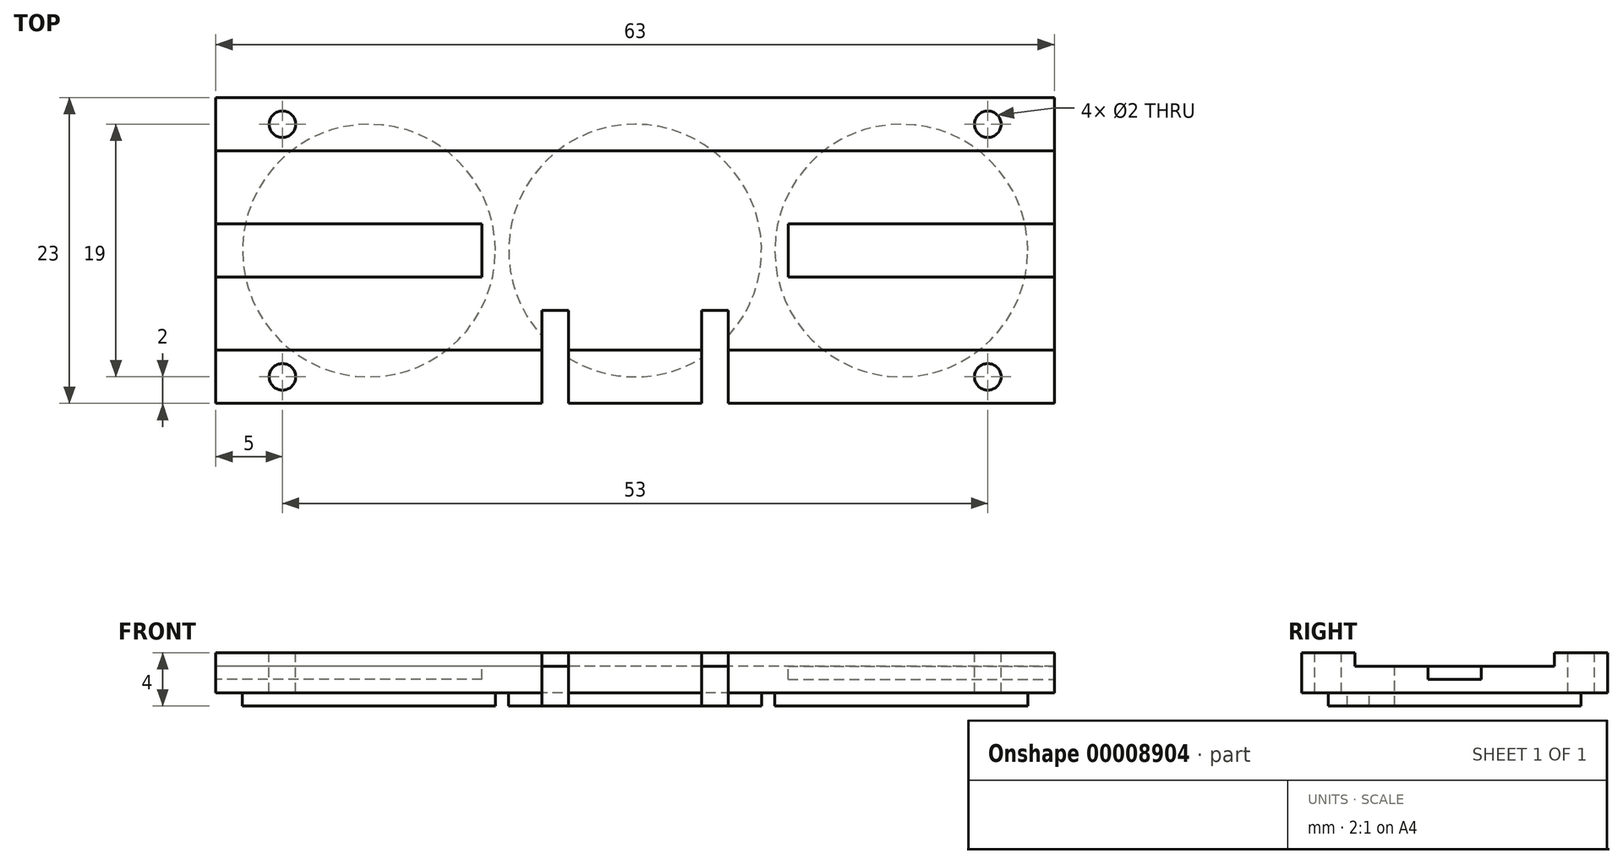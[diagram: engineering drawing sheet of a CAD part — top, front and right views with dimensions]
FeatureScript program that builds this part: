
annotation { "Feature Type Name" : "Feature", "Feature Type Description" : "" }
export const myFeature = defineFeature(function(context is Context, id is Id, definition is map)
    precondition{}
    {
        {
            var Q0;
            Q0=qCreatedBy(makeId("Top.planeOp"),FACE);
            var sketch = newSketch(context, id + "F0", { "sketchPlane" : qUnion([Q0])});
            skLineSegment(sketch, "E0.0", {"start": v(0, 12) * mm, "end": v(-32, 12) * mm, "construction": true});
            skLineSegment(sketch, "E1.0", {"start": v(0, 12) * mm, "end": v(32, 12) * mm, "construction": true});
            skLineSegment(sketch, "E2.0", {"start": v(0, -12) * mm, "end": v(-32, -12) * mm, "construction": true});
            skLineSegment(sketch, "E3.0", {"start": v(0, -12) * mm, "end": v(32, -12) * mm, "construction": true});
            skLineSegment(sketch, "E4", {"start": v(-32, 12) * mm, "end": v(-32, -12) * mm, "construction": true});
            skLineSegment(sketch, "E5", {"start": v(32, 12) * mm, "end": v(32, -12) * mm, "construction": true});
            skCircle(sketch, "E6", {"center": v(0, 0) * mm, "radius": 10 * mm, "construction": true});
            skLineSegment(sketch, "E7", {"start": v(0, 0) * mm, "end": v(-20, 0) * mm, "construction": true});
            skLineSegment(sketch, "E8", {"start": v(0, 0) * mm, "end": v(20, 0) * mm, "construction": true});
            skCircle(sketch, "E9", {"center": v(-20, 0) * mm, "radius": 10 * mm, "construction": true});
            skCircle(sketch, "E10", {"center": v(20, 0) * mm, "radius": 10 * mm, "construction": true});
            skLineSegment(sketch, "E11.0", {"start": v(-31.5, 12) * mm, "end": v(-31.5, -12) * mm});
            skLineSegment(sketch, "E12.0", {"start": v(31.5, 12) * mm, "end": v(31.5, -12) * mm});
            skLineSegment(sketch, "E13.0", {"start": v(0, 11.5) * mm, "end": v(32, 11.5) * mm});
            skLineSegment(sketch, "E14.0", {"start": v(0, 11.5) * mm, "end": v(-32, 11.5) * mm});
            skLineSegment(sketch, "E15.0", {"start": v(0, -11.5) * mm, "end": v(32, -11.5) * mm});
            skLineSegment(sketch, "E16.0", {"start": v(0, -11.5) * mm, "end": v(-32, -11.5) * mm});
            skLineSegment(sketch, "E17.0", {"start": v(32, -5) * mm, "end": v(31.5, -5) * mm});
            skLineSegment(sketch, "E18.trimOffspring", {"start": v(-31.5, 5) * mm, "end": v(-32, 5) * mm});
            skLineSegment(sketch, "E19.trimOffspring", {"start": v(-8.08, -5) * mm, "end": v(-11.92, -5) * mm});
            skLineSegment(sketch, "E20.trimOffspring", {"start": v(-8.08, 5) * mm, "end": v(-11.92, 5) * mm});
            skLineSegment(sketch, "E21.trimOffspring", {"start": v(11.92, 5) * mm, "end": v(8.08, 5) * mm});
            skLineSegment(sketch, "E22.trimOffspring", {"start": v(11.92, -5) * mm, "end": v(8.08, -5) * mm});
            skCircle(sketch, "E23.0", {"center": v(-20, 0) * mm, "radius": 9.5 * mm});
            skCircle(sketch, "E24.0", {"center": v(0, 0) * mm, "radius": 9.5 * mm});
            skCircle(sketch, "E25.0", {"center": v(20, 0) * mm, "radius": 9.5 * mm});
            skSolve(sketch);
        }
        {
            var Q0;
            {var subQ13=sQuery(id+"F0.wireOp",EDGE,"E19.trimOffspring");Q0=makeQuery(id+"F0.imprint","IMPRINT",FACE,{"disambiguationData":[TD([[makeQuery(id+"F0.imprint","IMPRINT",EDGE,{"derivedFrom":subQ13}),1.0]])]});}
            var Q1;
            {var subQ0=sQuery(id+"F0.wireOp",EDGE,"E9");var subQ3=makeQuery(id+"F0.imprint","INTERSECT",VERTEX,{"derivedFrom":[subQ0,sQuery(id+"F0.wireOp",EDGE,"E20.trimOffspring")]});Q1=makeQuery(id+"F0.imprint","IMPRINT",FACE,{"disambiguationData":[TD([[makeQuery(id+"F0.imprint","IMPRINT",EDGE,{"disambiguationData":[TD([[subQ3,1.0]])],"derivedFrom":subQ0}),1.0]])]});}
            var Q2;
            {var subQ0=sQuery(id+"F0.wireOp",EDGE,"E20.trimOffspring");Q2=makeQuery(id+"F0.imprint","IMPRINT",FACE,{"disambiguationData":[TD([[makeQuery(id+"F0.imprint","IMPRINT",EDGE,{"derivedFrom":subQ0}),1.0]])]});}
            var Q3;
            {var subQ0=sQuery(id+"F0.wireOp",EDGE,"E19.trimOffspring");Q3=makeQuery(id+"F0.imprint","IMPRINT",FACE,{"disambiguationData":[TD([[makeQuery(id+"F0.imprint","IMPRINT",EDGE,{"derivedFrom":subQ0}),-1.0]])]});}
            var Q4;
            {var subQ0=sQuery(id+"F0.wireOp",EDGE,"E6");var subQ6=makeQuery(id+"F0.imprint","INTERSECT",VERTEX,{"derivedFrom":[subQ0,sQuery(id+"F0.wireOp",EDGE,"E21.trimOffspring")]});Q4=makeQuery(id+"F0.imprint","IMPRINT",FACE,{"disambiguationData":[TD([[makeQuery(id+"F0.imprint","IMPRINT",EDGE,{"disambiguationData":[TD([[subQ6,1.0]])],"derivedFrom":subQ0}),1.0]])]});}
            var Q5;
            {var subQ0=sQuery(id+"F0.wireOp",EDGE,"E21.trimOffspring");Q5=makeQuery(id+"F0.imprint","IMPRINT",FACE,{"disambiguationData":[TD([[makeQuery(id+"F0.imprint","IMPRINT",EDGE,{"derivedFrom":subQ0}),1.0]])]});}
            var Q6;
            {var subQ0=sQuery(id+"F0.wireOp",EDGE,"E22.trimOffspring");Q6=makeQuery(id+"F0.imprint","IMPRINT",FACE,{"disambiguationData":[TD([[makeQuery(id+"F0.imprint","IMPRINT",EDGE,{"derivedFrom":subQ0}),-1.0]])]});}
            var Q7;
            {var subQ0=sQuery(id+"F0.wireOp",EDGE,"E10");var subQ2=makeQuery(id+"F0.imprint","INTERSECT",VERTEX,{"derivedFrom":[subQ0,sQuery(id+"F0.wireOp",EDGE,"E21.trimOffspring")]});Q7=makeQuery(id+"F0.imprint","IMPRINT",FACE,{"disambiguationData":[TD([[makeQuery(id+"F0.imprint","IMPRINT",EDGE,{"disambiguationData":[TD([[subQ2,-1.0]])],"derivedFrom":subQ0}),1.0]])]});}
            var Q8;
            {var subQ0=sQuery(id+"F0.wireOp",EDGE,"E23.0");var subQ2=makeQuery(id+"F0.imprint","INTERSECT",VERTEX,{"derivedFrom":[sQuery(id+"F0.wireOp",EDGE,"E19.trimOffspring"),subQ0]});Q8=makeQuery(id+"F0.imprint","IMPRINT",FACE,{"disambiguationData":[TD([[makeQuery(id+"F0.imprint","IMPRINT",EDGE,{"disambiguationData":[TD([[subQ2,1.0]])],"derivedFrom":subQ0}),1.0]])]});}
            var Q9;
            {var subQ0=sQuery(id+"F0.wireOp",EDGE,"E24.0");var subQ4=makeQuery(id+"F0.imprint","INTERSECT",VERTEX,{"derivedFrom":[sQuery(id+"F0.wireOp",EDGE,"E20.trimOffspring"),subQ0]});Q9=makeQuery(id+"F0.imprint","IMPRINT",FACE,{"disambiguationData":[TD([[makeQuery(id+"F0.imprint","IMPRINT",EDGE,{"disambiguationData":[TD([[subQ4,1.0]])],"derivedFrom":subQ0}),1.0]])]});}
            var Q10;
            {var subQ0=sQuery(id+"F0.wireOp",EDGE,"E25.0");var subQ2=makeQuery(id+"F0.imprint","INTERSECT",VERTEX,{"derivedFrom":[sQuery(id+"F0.wireOp",EDGE,"E21.trimOffspring"),subQ0]});Q10=makeQuery(id+"F0.imprint","IMPRINT",FACE,{"disambiguationData":[TD([[makeQuery(id+"F0.imprint","IMPRINT",EDGE,{"disambiguationData":[TD([[subQ2,-1.0]])],"derivedFrom":subQ0}),1.0]])]});}
            extrude(context, id + "F1", {"entities" : qUnion([Q0, Q1, Q2, Q3, Q4, Q5, Q6, Q7, Q8, Q9, Q10]), "depth" : 2 * mm});
        }
        {
            var Q0;
            {var subQ0=sQuery(id+"F0.wireOp",EDGE,"E9");var subQ3=makeQuery(id+"F0.imprint","INTERSECT",VERTEX,{"derivedFrom":[subQ0,sQuery(id+"F0.wireOp",EDGE,"E20.trimOffspring")]});Q0=makeQuery(id+"F0.imprint","IMPRINT",FACE,{"disambiguationData":[TD([[makeQuery(id+"F0.imprint","IMPRINT",EDGE,{"disambiguationData":[TD([[subQ3,1.0]])],"derivedFrom":subQ0}),1.0]])]});}
            var Q1;
            {var subQ0=sQuery(id+"F0.wireOp",EDGE,"E6");var subQ6=makeQuery(id+"F0.imprint","INTERSECT",VERTEX,{"derivedFrom":[subQ0,sQuery(id+"F0.wireOp",EDGE,"E21.trimOffspring")]});Q1=makeQuery(id+"F0.imprint","IMPRINT",FACE,{"disambiguationData":[TD([[makeQuery(id+"F0.imprint","IMPRINT",EDGE,{"disambiguationData":[TD([[subQ6,1.0]])],"derivedFrom":subQ0}),1.0]])]});}
            var Q2;
            {var subQ0=sQuery(id+"F0.wireOp",EDGE,"E10");var subQ2=makeQuery(id+"F0.imprint","INTERSECT",VERTEX,{"derivedFrom":[subQ0,sQuery(id+"F0.wireOp",EDGE,"E21.trimOffspring")]});Q2=makeQuery(id+"F0.imprint","IMPRINT",FACE,{"disambiguationData":[TD([[makeQuery(id+"F0.imprint","IMPRINT",EDGE,{"disambiguationData":[TD([[subQ2,-1.0]])],"derivedFrom":subQ0}),1.0]])]});}
            var Q3;
            {var subQ0=sQuery(id+"F0.wireOp",EDGE,"E23.0");var subQ2=makeQuery(id+"F0.imprint","INTERSECT",VERTEX,{"derivedFrom":[sQuery(id+"F0.wireOp",EDGE,"E19.trimOffspring"),subQ0]});Q3=makeQuery(id+"F0.imprint","IMPRINT",FACE,{"disambiguationData":[TD([[makeQuery(id+"F0.imprint","IMPRINT",EDGE,{"disambiguationData":[TD([[subQ2,1.0]])],"derivedFrom":subQ0}),1.0]])]});}
            var Q4;
            {var subQ0=sQuery(id+"F0.wireOp",EDGE,"E24.0");var subQ4=makeQuery(id+"F0.imprint","INTERSECT",VERTEX,{"derivedFrom":[sQuery(id+"F0.wireOp",EDGE,"E20.trimOffspring"),subQ0]});Q4=makeQuery(id+"F0.imprint","IMPRINT",FACE,{"disambiguationData":[TD([[makeQuery(id+"F0.imprint","IMPRINT",EDGE,{"disambiguationData":[TD([[subQ4,1.0]])],"derivedFrom":subQ0}),1.0]])]});}
            var Q5;
            {var subQ0=sQuery(id+"F0.wireOp",EDGE,"E25.0");var subQ2=makeQuery(id+"F0.imprint","INTERSECT",VERTEX,{"derivedFrom":[sQuery(id+"F0.wireOp",EDGE,"E21.trimOffspring"),subQ0]});Q5=makeQuery(id+"F0.imprint","IMPRINT",FACE,{"disambiguationData":[TD([[makeQuery(id+"F0.imprint","IMPRINT",EDGE,{"disambiguationData":[TD([[subQ2,-1.0]])],"derivedFrom":subQ0}),1.0]])]});}
            extrude(context, id + "F2", {"entities" : qUnion([Q0, Q1, Q2, Q3, Q4, Q5]), "operationType" : NewBodyOperationType.ADD, "oppositeDirection" : true, "depth" : 3 * mm});
        }
        {
            var Q0;
            Q0=makeQuery(id+"F1.opExtrude","CAP_FACE",FACE,{"disambiguationData":[OSD([sQuery(id+"F0.wireOp",EDGE,"E11.0"),sQuery(id+"F0.wireOp",EDGE,"E12.0"),sQuery(id+"F0.wireOp",EDGE,"E13.0"),sQuery(id+"F0.wireOp",EDGE,"E14.0"),sQuery(id+"F0.wireOp",EDGE,"E15.0"),sQuery(id+"F0.wireOp",EDGE,"E16.0")])],"isStart":true});
            extrude(context, id + "F3", {"entities" : qUnion([Q0]), "operationType" : NewBodyOperationType.ADD, "depth" : 2 * mm});
        }
        {
            var Q0;
            Q0=makeQuery(id+"F1.opExtrude","CAP_FACE",FACE,{"disambiguationData":[OSD([sQuery(id+"F0.wireOp",EDGE,"E11.0"),sQuery(id+"F0.wireOp",EDGE,"E12.0"),sQuery(id+"F0.wireOp",EDGE,"E13.0"),sQuery(id+"F0.wireOp",EDGE,"E14.0"),sQuery(id+"F0.wireOp",EDGE,"E15.0"),sQuery(id+"F0.wireOp",EDGE,"E16.0")])],"isStart":false});
            extrude(context, id + "F4", {"entities" : qUnion([Q0]), "operationType" : NewBodyOperationType.REMOVE, "oppositeDirection" : true, "depth" : 1 * mm});
        }
        {
            var Q0;
            Q0=makeQuery(id+"F4.boolean.opBoolean","COPY",FACE,{"derivedFrom":makeQuery(id+"F4.opExtrude","CAP_FACE",FACE,{"disambiguationData":[OSD([sQuery(id+"F0.wireOp",EDGE,"E11.0"),sQuery(id+"F0.wireOp",EDGE,"E12.0"),sQuery(id+"F0.wireOp",EDGE,"E13.0"),sQuery(id+"F0.wireOp",EDGE,"E14.0"),sQuery(id+"F0.wireOp",EDGE,"E15.0"),sQuery(id+"F0.wireOp",EDGE,"E16.0")])],"isStart":false})});
            var sketch = newSketch(context, id + "F5", { "sketchPlane" : qUnion([Q0])});
            skLineSegment(sketch, "E26.0", {"start": v(11.5, 11.5) * mm, "end": v(11.5, -11.5) * mm});
            skLineSegment(sketch, "E27.0", {"start": v(-11.5, 11.5) * mm, "end": v(-11.5, -11.5) * mm});
            skLineSegment(sketch, "E28", {"start": v(-11.5, 0) * mm, "end": v(-31.5, 0) * mm});
            skLineSegment(sketch, "E29", {"start": v(11.5, 0) * mm, "end": v(31.5, 0) * mm});
            skLineSegment(sketch, "E30.0", {"start": v(0, 5) * mm, "end": v(-31.5, 5) * mm, "construction": true});
            skLineSegment(sketch, "E31.0", {"start": v(0, -5) * mm, "end": v(-31.5, -5) * mm, "construction": true});
            skLineSegment(sketch, "E32.0", {"start": v(0, -5) * mm, "end": v(31.5, -5) * mm, "construction": true});
            skLineSegment(sketch, "E33.0", {"start": v(0, 5) * mm, "end": v(31.5, 5) * mm, "construction": true});
            skLineSegment(sketch, "E34.0", {"start": v(-11.5, 2) * mm, "end": v(-31.5, 2) * mm});
            skLineSegment(sketch, "E35.0", {"start": v(-11.5, -2) * mm, "end": v(-31.5, -2) * mm});
            skLineSegment(sketch, "E36.0", {"start": v(11.5, -2) * mm, "end": v(31.5, -2) * mm});
            skLineSegment(sketch, "E37.0", {"start": v(11.5, 2) * mm, "end": v(31.5, 2) * mm});
            skSolve(sketch);
        }
        {
            var Q0;
            {var subQ2=sQuery(id+"F5.wireOp",EDGE,"E28");Q0=makeQuery(id+"F5.imprint","IMPRINT",FACE,{"disambiguationData":[TD([[makeQuery(id+"F5.imprint","IMPRINT",EDGE,{"derivedFrom":subQ2}),1.0]])]});}
            var Q1;
            {var subQ2=sQuery(id+"F5.wireOp",EDGE,"E28");Q1=makeQuery(id+"F5.imprint","IMPRINT",FACE,{"disambiguationData":[TD([[makeQuery(id+"F5.imprint","IMPRINT",EDGE,{"derivedFrom":subQ2}),-1.0]])]});}
            var Q2;
            {var subQ2=sQuery(id+"F5.wireOp",EDGE,"E29");Q2=makeQuery(id+"F5.imprint","IMPRINT",FACE,{"disambiguationData":[TD([[makeQuery(id+"F5.imprint","IMPRINT",EDGE,{"derivedFrom":subQ2}),1.0]])]});}
            var Q3;
            {var subQ2=sQuery(id+"F5.wireOp",EDGE,"E29");Q3=makeQuery(id+"F5.imprint","IMPRINT",FACE,{"disambiguationData":[TD([[makeQuery(id+"F5.imprint","IMPRINT",EDGE,{"derivedFrom":subQ2}),-1.0]])]});}
            extrude(context, id + "F6", {"entities" : qUnion([Q0, Q1, Q2, Q3]), "operationType" : NewBodyOperationType.REMOVE, "oppositeDirection" : true, "depth" : 2 * mm});
        }
        {
            var Q0;
            Q0=makeQuery(id+"F4.boolean.opBoolean","COPY",FACE,{"derivedFrom":makeQuery(id+"F4.opExtrude","CAP_FACE",FACE,{"disambiguationData":[OSD([sQuery(id+"F0.wireOp",EDGE,"E11.0"),sQuery(id+"F0.wireOp",EDGE,"E12.0"),sQuery(id+"F0.wireOp",EDGE,"E13.0"),sQuery(id+"F0.wireOp",EDGE,"E14.0"),sQuery(id+"F0.wireOp",EDGE,"E15.0"),sQuery(id+"F0.wireOp",EDGE,"E16.0")])],"isStart":false})});
            var sketch = newSketch(context, id + "F7", { "sketchPlane" : qUnion([Q0])});
            skLineSegment(sketch, "E38.0", {"start": v(31.5, 7.5) * mm, "end": v(-31.5, 7.5) * mm});
            skLineSegment(sketch, "E39.0", {"start": v(31.5, -7.5) * mm, "end": v(-31.5, -7.5) * mm});
            skSolve(sketch);
        }
        {
            var Q0;
            {var subQ20=sQuery(id+"F7.wireOp",EDGE,"E38.0");Q0=makeQuery(id+"F7.imprint","IMPRINT",FACE,{"disambiguationData":[TD([[makeQuery(id+"F7.imprint","IMPRINT",EDGE,{"derivedFrom":subQ20}),1.0]])]});}
            extrude(context, id + "F8", {"entities" : qUnion([Q0]), "operationType" : NewBodyOperationType.REMOVE, "oppositeDirection" : true, "depth" : 1 * mm});
        }
        {
            var Q0;
            {var subQ0=sQuery(id+"F0.wireOp",EDGE,"E11.0");var subQ1=sQuery(id+"F0.wireOp",EDGE,"E12.0");var subQ2=sQuery(id+"F0.wireOp",EDGE,"E15.0");var subQ3=sQuery(id+"F0.wireOp",EDGE,"E16.0");Q0=makeQuery(id+"F8.boolean.opBoolean","SPLIT",FACE,{"disambiguationData":[TD([makeQuery(id+"F8.opExtrude","SWEPT_FACE",FACE,{"disambiguationData":[OSD([sQuery(id+"F7.wireOp",EDGE,"E39.0")])]})])],"derivedFrom":makeQuery(id+"F4.boolean.opBoolean","COPY",FACE,{"derivedFrom":makeQuery(id+"F4.opExtrude","CAP_FACE",FACE,{"disambiguationData":[OSD([subQ0,subQ1,sQuery(id+"F0.wireOp",EDGE,"E13.0"),sQuery(id+"F0.wireOp",EDGE,"E14.0"),subQ2,subQ3])],"isStart":false})})});}
            var sketch = newSketch(context, id + "F9", { "sketchPlane" : qUnion([Q0])});
            skLineSegment(sketch, "E40", {"start": v(0, -6.5) * mm, "end": v(0, -13.86) * mm});
            skLineSegment(sketch, "E41.0", {"start": v(31.5, -11.5) * mm, "end": v(-31.5, -11.5) * mm});
            skLineSegment(sketch, "E42.0", {"start": v(-5, -4.5) * mm, "end": v(-5, -13.86) * mm});
            skLineSegment(sketch, "E43.0", {"start": v(5, -4.5) * mm, "end": v(5, -13.86) * mm});
            skLineSegment(sketch, "E44.0", {"start": v(-7, -4.5) * mm, "end": v(-7, -13.86) * mm});
            skLineSegment(sketch, "E45.0", {"start": v(7, -4.5) * mm, "end": v(7, -13.86) * mm});
            skLineSegment(sketch, "E46.0", {"start": v(31.5, -6.5) * mm, "end": v(-31.5, -6.5) * mm});
            skLineSegment(sketch, "E47.0", {"start": v(31.5, -4.5) * mm, "end": v(-31.5, -4.5) * mm});
            skSolve(sketch);
        }
        {
            var Q0;
            {var subQ1=sQuery(id+"F9.wireOp",EDGE,"E42.0");var subQ5=sQuery(id+"F9.wireOp",EDGE,"E46.0");var subQ7=makeQuery(id+"F9.imprint","INTERSECT",VERTEX,{"derivedFrom":[subQ1,subQ5]});Q0=makeQuery(id+"F9.imprint","IMPRINT",FACE,{"disambiguationData":[TD([[makeQuery(id+"F9.imprint","IMPRINT",EDGE,{"disambiguationData":[TD([[subQ7,-1.0]])],"derivedFrom":subQ1}),-1.0]])]});}
            var Q1;
            {var subQ1=sQuery(id+"F9.wireOp",EDGE,"E42.0");var subQ5=sQuery(id+"F9.wireOp",EDGE,"E41.0");var subQ7=makeQuery(id+"F9.imprint","INTERSECT",VERTEX,{"derivedFrom":[subQ5,subQ1]});Q1=makeQuery(id+"F9.imprint","IMPRINT",FACE,{"disambiguationData":[TD([[makeQuery(id+"F9.imprint","IMPRINT",EDGE,{"disambiguationData":[TD([[subQ7,-1.0]])],"derivedFrom":subQ5}),-1.0]])]});}
            var Q2;
            {var subQ1=sQuery(id+"F9.wireOp",EDGE,"E43.0");var subQ5=sQuery(id+"F9.wireOp",EDGE,"E46.0");var subQ7=makeQuery(id+"F9.imprint","INTERSECT",VERTEX,{"derivedFrom":[subQ1,subQ5]});Q2=makeQuery(id+"F9.imprint","IMPRINT",FACE,{"disambiguationData":[TD([[makeQuery(id+"F9.imprint","IMPRINT",EDGE,{"disambiguationData":[TD([[subQ7,-1.0]])],"derivedFrom":subQ1}),1.0]])]});}
            var Q3;
            {var subQ3=sQuery(id+"F9.wireOp",EDGE,"E45.0");var subQ5=sQuery(id+"F9.wireOp",EDGE,"E41.0");var subQ6=makeQuery(id+"F9.imprint","INTERSECT",VERTEX,{"derivedFrom":[subQ5,subQ3]});Q3=makeQuery(id+"F9.imprint","IMPRINT",FACE,{"disambiguationData":[TD([[makeQuery(id+"F9.imprint","IMPRINT",EDGE,{"disambiguationData":[TD([[subQ6,-1.0]])],"derivedFrom":subQ5}),-1.0]])]});}
            var Q4;
            {var subQ0=sQuery(id+"F9.wireOp",EDGE,"E47.0");var subQ3=sQuery(id+"F9.wireOp",EDGE,"E42.0");var subQ4=makeQuery(id+"F9.imprint","INTERSECT",VERTEX,{"derivedFrom":[subQ3,subQ0]});Q4=makeQuery(id+"F9.imprint","IMPRINT",FACE,{"disambiguationData":[TD([[makeQuery(id+"F9.imprint","IMPRINT",EDGE,{"disambiguationData":[TD([[subQ4,-1.0]])],"derivedFrom":subQ3}),-1.0]])]});}
            var Q5;
            {var subQ0=sQuery(id+"F9.wireOp",EDGE,"E47.0");var subQ3=sQuery(id+"F9.wireOp",EDGE,"E43.0");var subQ4=makeQuery(id+"F9.imprint","INTERSECT",VERTEX,{"derivedFrom":[subQ3,subQ0]});Q5=makeQuery(id+"F9.imprint","IMPRINT",FACE,{"disambiguationData":[TD([[makeQuery(id+"F9.imprint","IMPRINT",EDGE,{"disambiguationData":[TD([[subQ4,-1.0]])],"derivedFrom":subQ3}),1.0]])]});}
            extrude(context, id + "F10", {"entities" : qUnion([Q0, Q1, Q2, Q3, Q4, Q5]), "operationType" : NewBodyOperationType.REMOVE, "oppositeDirection" : true, "depth" : 25 * mm});
        }
        {
            var Q0;
            {var subQ0=sQuery(id+"F0.wireOp",EDGE,"E11.0");var subQ1=sQuery(id+"F0.wireOp",EDGE,"E12.0");var subQ2=sQuery(id+"F0.wireOp",EDGE,"E15.0");var subQ3=sQuery(id+"F0.wireOp",EDGE,"E16.0");var subQ4=makeQuery(id+"F8.opExtrude","SWEPT_FACE",FACE,{"disambiguationData":[OSD([sQuery(id+"F7.wireOp",EDGE,"E39.0")])]});var subQ8=makeQuery(id+"F1.opExtrude","SWEPT_FACE",FACE,{"disambiguationData":[OSD([subQ0])]});Q0=makeQuery(id+"F10.boolean.opBoolean","SPLIT",FACE,{"disambiguationData":[TD([subQ8])],"derivedFrom":makeQuery(id+"F8.boolean.opBoolean","SPLIT",FACE,{"disambiguationData":[TD([subQ4])],"derivedFrom":makeQuery(id+"F4.boolean.opBoolean","COPY",FACE,{"derivedFrom":makeQuery(id+"F4.opExtrude","CAP_FACE",FACE,{"disambiguationData":[OSD([subQ0,subQ1,sQuery(id+"F0.wireOp",EDGE,"E13.0"),sQuery(id+"F0.wireOp",EDGE,"E14.0"),subQ2,subQ3])],"isStart":false})})})});}
            var sketch = newSketch(context, id + "F11", { "sketchPlane" : qUnion([Q0])});
            skLineSegment(sketch, "E48", {"start": v(-31.5, -11.5) * mm, "end": v(-26.5, -11.5) * mm});
            skLineSegment(sketch, "E49.0", {"start": v(-31.5, -9.5) * mm, "end": v(-26.5, -9.5) * mm});
            skCircle(sketch, "E50", {"center": v(-26.5, -9.5) * mm, "radius": 1 * mm});
            skSolve(sketch);
        }
        {
            var Q0;
            {var subQ0=sQuery(id+"F0.wireOp",EDGE,"E11.0");var subQ1=sQuery(id+"F0.wireOp",EDGE,"E12.0");var subQ2=sQuery(id+"F0.wireOp",EDGE,"E13.0");var subQ3=sQuery(id+"F0.wireOp",EDGE,"E14.0");Q0=makeQuery(id+"F8.boolean.opBoolean","SPLIT",FACE,{"disambiguationData":[TD([makeQuery(id+"F8.opExtrude","SWEPT_FACE",FACE,{"disambiguationData":[OSD([sQuery(id+"F7.wireOp",EDGE,"E38.0")])]})])],"derivedFrom":makeQuery(id+"F4.boolean.opBoolean","COPY",FACE,{"derivedFrom":makeQuery(id+"F4.opExtrude","CAP_FACE",FACE,{"disambiguationData":[OSD([subQ0,subQ1,subQ2,subQ3,sQuery(id+"F0.wireOp",EDGE,"E15.0"),sQuery(id+"F0.wireOp",EDGE,"E16.0")])],"isStart":false})})});}
            var sketch = newSketch(context, id + "F12", { "sketchPlane" : qUnion([Q0])});
            skLineSegment(sketch, "E51", {"start": v(-31.5, 11.5) * mm, "end": v(-26.5, 11.5) * mm});
            skLineSegment(sketch, "E52.0", {"start": v(-31.5, 9.5) * mm, "end": v(-26.5, 9.5) * mm});
            skCircle(sketch, "E53", {"center": v(-26.5, 9.5) * mm, "radius": 1 * mm});
            skLineSegment(sketch, "E54", {"start": v(31.5, 11.5) * mm, "end": v(26.5, 11.5) * mm});
            skLineSegment(sketch, "E55.0", {"start": v(31.5, 9.5) * mm, "end": v(26.5, 9.5) * mm});
            skCircle(sketch, "E56", {"center": v(26.5, 9.5) * mm, "radius": 1 * mm});
            skSolve(sketch);
        }
        {
            var Q0;
            {var subQ0=sQuery(id+"F0.wireOp",EDGE,"E11.0");var subQ1=sQuery(id+"F0.wireOp",EDGE,"E12.0");var subQ2=sQuery(id+"F0.wireOp",EDGE,"E15.0");var subQ3=sQuery(id+"F0.wireOp",EDGE,"E16.0");var subQ4=makeQuery(id+"F8.opExtrude","SWEPT_FACE",FACE,{"disambiguationData":[OSD([sQuery(id+"F7.wireOp",EDGE,"E39.0")])]});var subQ8=makeQuery(id+"F1.opExtrude","SWEPT_FACE",FACE,{"disambiguationData":[OSD([subQ1])]});Q0=makeQuery(id+"F10.boolean.opBoolean","SPLIT",FACE,{"disambiguationData":[TD([subQ8])],"derivedFrom":makeQuery(id+"F8.boolean.opBoolean","SPLIT",FACE,{"disambiguationData":[TD([subQ4])],"derivedFrom":makeQuery(id+"F4.boolean.opBoolean","COPY",FACE,{"derivedFrom":makeQuery(id+"F4.opExtrude","CAP_FACE",FACE,{"disambiguationData":[OSD([subQ0,subQ1,sQuery(id+"F0.wireOp",EDGE,"E13.0"),sQuery(id+"F0.wireOp",EDGE,"E14.0"),subQ2,subQ3])],"isStart":false})})})});}
            var sketch = newSketch(context, id + "F13", { "sketchPlane" : qUnion([Q0])});
            skLineSegment(sketch, "E57", {"start": v(31.5, -11.5) * mm, "end": v(26.5, -11.5) * mm});
            skLineSegment(sketch, "E58.0", {"start": v(31.5, -9.5) * mm, "end": v(26.5, -9.5) * mm});
            skCircle(sketch, "E59", {"center": v(26.5, -9.5) * mm, "radius": 1 * mm});
            skSolve(sketch);
        }
        {
            var Q0;
            Q0=makeQuery(id+"F12.imprint","IMPRINT",FACE,{"disambiguationData":[TD([[makeQuery(id+"F12.imprint","IMPRINT",EDGE,{"derivedFrom":sQuery(id+"F12.wireOp",EDGE,"E53")}),1.0]])]});
            var Q1;
            Q1=makeQuery(id+"F11.imprint","IMPRINT",FACE,{"disambiguationData":[TD([[makeQuery(id+"F11.imprint","IMPRINT",EDGE,{"derivedFrom":sQuery(id+"F11.wireOp",EDGE,"E50")}),1.0]])]});
            var Q2;
            Q2=makeQuery(id+"F13.imprint","IMPRINT",FACE,{"disambiguationData":[TD([[makeQuery(id+"F13.imprint","IMPRINT",EDGE,{"derivedFrom":sQuery(id+"F13.wireOp",EDGE,"E59")}),1.0]])]});
            var Q3;
            Q3=makeQuery(id+"F12.imprint","IMPRINT",FACE,{"disambiguationData":[TD([[makeQuery(id+"F12.imprint","IMPRINT",EDGE,{"derivedFrom":sQuery(id+"F12.wireOp",EDGE,"E56")}),1.0]])]});
            extrude(context, id + "F14", {"entities" : qUnion([Q0, Q1, Q2, Q3]), "operationType" : NewBodyOperationType.REMOVE, "oppositeDirection" : true, "depth" : 25 * mm});
        }
    });
